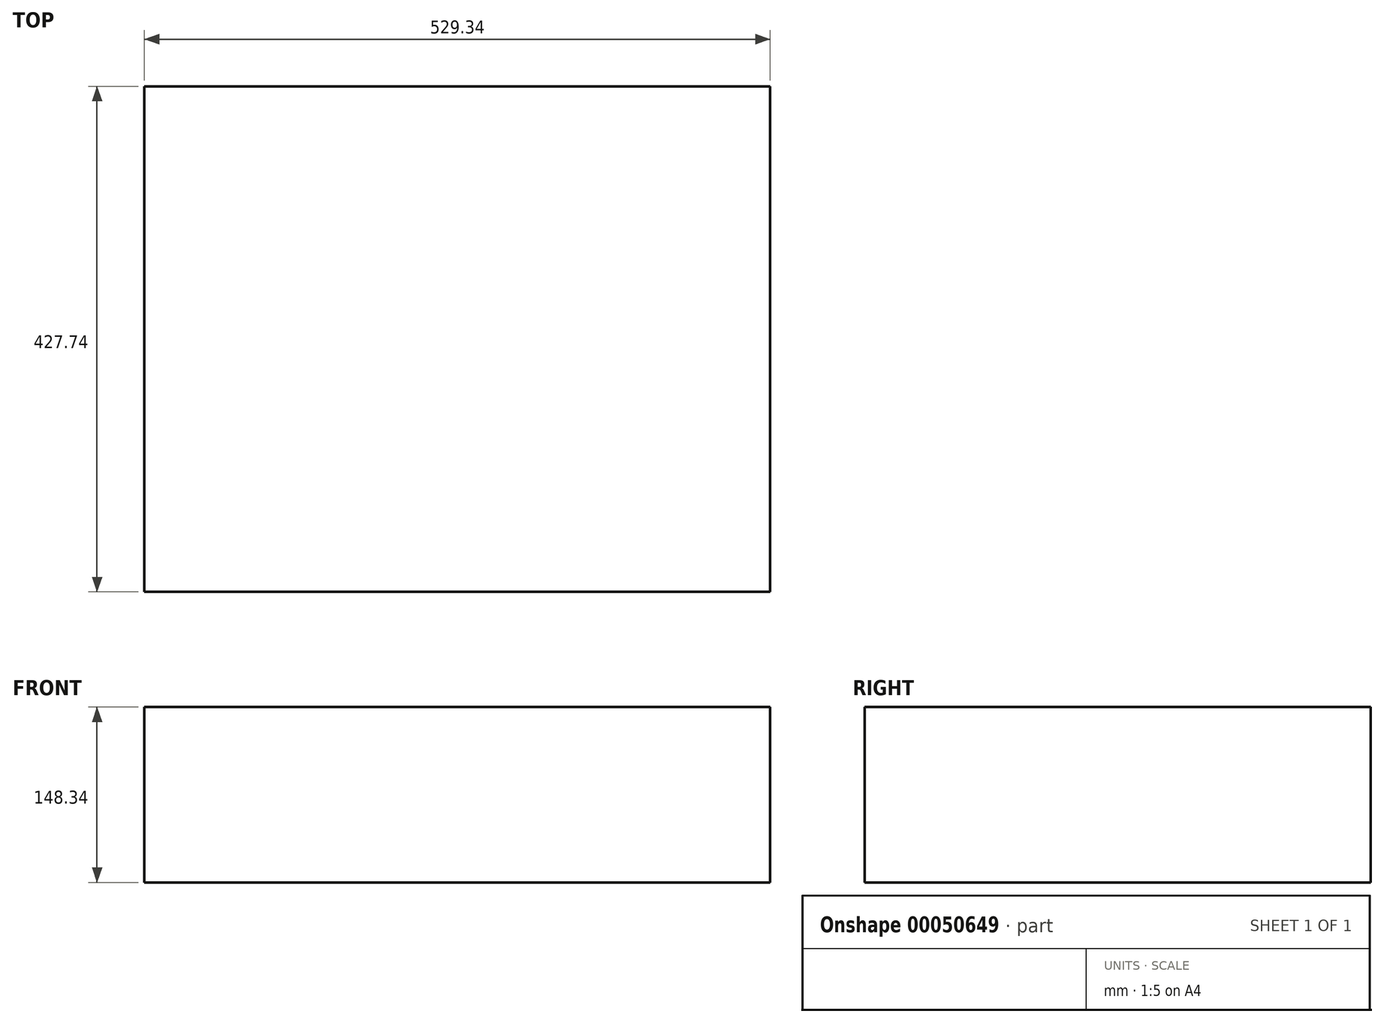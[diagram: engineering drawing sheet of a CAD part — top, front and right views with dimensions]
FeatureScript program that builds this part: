
annotation { "Feature Type Name" : "Feature", "Feature Type Description" : "" }
export const myFeature = defineFeature(function(context is Context, id is Id, definition is map)
    precondition{}
    {
        {
            var Q0;
            Q0=qCreatedBy(makeId("Top.planeOp"),FACE);
            var sketch = newSketch(context, id + "F0", { "sketchPlane" : qUnion([Q0])});
            skLineSegment(sketch, "E0.bottom", {"start": v(0, 0) * mm, "end": v(529.34, 0) * mm});
            skLineSegment(sketch, "E0.top", {"start": v(0, 427.74) * mm, "end": v(529.34, 427.74) * mm});
            skLineSegment(sketch, "E0.left", {"start": v(0, 0) * mm, "end": v(0, 427.74) * mm});
            skLineSegment(sketch, "E0.right", {"start": v(529.34, 0) * mm, "end": v(529.34, 427.74) * mm});
            skSolve(sketch);
        }
        {
            var Q0;
            Q0=makeQuery(id+"F0.imprint","IMPRINT",FACE,{"disambiguationData":[TD([[makeQuery(id+"F0.imprint","IMPRINT",EDGE,{"derivedFrom":sQuery(id+"F0.wireOp",EDGE,"E0.bottom")}),1.0]])]});
            extrude(context, id + "F1", {"entities" : qUnion([Q0]), "depth" : 148.34 * mm});
        }
    });
